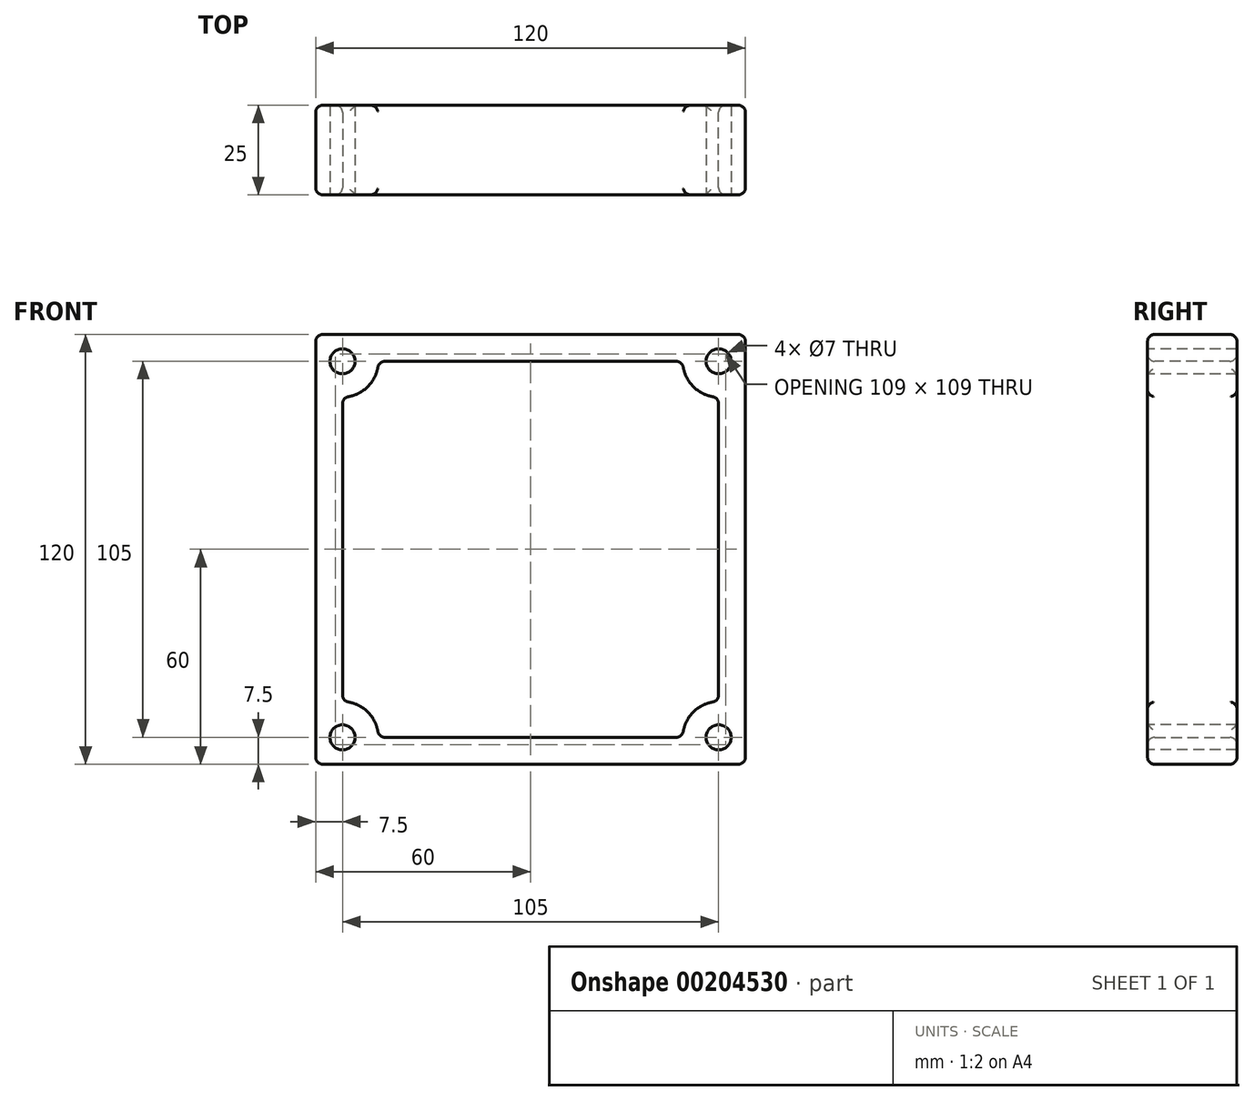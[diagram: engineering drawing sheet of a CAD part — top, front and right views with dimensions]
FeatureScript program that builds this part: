
annotation { "Feature Type Name" : "Feature", "Feature Type Description" : "" }
export const myFeature = defineFeature(function(context is Context, id is Id, definition is map)
    precondition{}
    {
        {
            var Q0;
            Q0=qCreatedBy(makeId("Front.planeOp"),FACE);
            var sketch = newSketch(context, id + "F0", { "sketchPlane" : qUnion([Q0])});
            skLineSegment(sketch, "E0", {"start": v(0, 36.07) * mm, "end": v(0, -63.9) * mm, "construction": true});
            skLineSegment(sketch, "E1", {"start": v(-89.54, 0) * mm, "end": v(99.03, 0) * mm, "construction": true});
            skLineSegment(sketch, "E2.bottom", {"start": v(60, 60) * mm, "end": v(-60, 60) * mm});
            skLineSegment(sketch, "E2.top", {"start": v(60, -60) * mm, "end": v(-60, -60) * mm});
            skLineSegment(sketch, "E2.left", {"start": v(60, 60) * mm, "end": v(60, -60) * mm});
            skLineSegment(sketch, "E2.right", {"start": v(-60, 60) * mm, "end": v(-60, -60) * mm});
            skPoint(sketch, "E2.middle", {"position": v(0, 0) * mm});
            skSolve(sketch);
        }
        {
            var Q0;
            Q0 = qSketchRegion(id + "F0", true);
            extrude(context, id + "F1", {"entities" : qUnion([Q0]), "depth" : 25 * mm});
        }
        {
            var Q0;
            Q0=makeQuery(id+"F1.opExtrude","CAP_FACE",FACE,{"disambiguationData":[OSD([sQuery(id+"F0.wireOp",EDGE,"E2.bottom"),sQuery(id+"F0.wireOp",EDGE,"E2.top"),sQuery(id+"F0.wireOp",EDGE,"E2.left"),sQuery(id+"F0.wireOp",EDGE,"E2.right")])],"isStart":false});
            var sketch = newSketch(context, id + "F2", { "sketchPlane" : qUnion([Q0])});
            skLineSegment(sketch, "E3", {"start": v(-77.64, 0) * mm, "end": v(91.45, 0) * mm, "construction": true});
            skLineSegment(sketch, "E4", {"start": v(0, 68.59) * mm, "end": v(0, -71.2) * mm, "construction": true});
            skCircle(sketch, "E5", {"center": v(-52.5, 52.5) * mm, "radius": 3.5 * mm});
            skCircle(sketch, "E6", {"center": v(-52.5, -52.5) * mm, "radius": 3.5 * mm});
            skCircle(sketch, "E7.MirrorC", {"center": v(52.5, -52.5) * mm, "radius": 3.5 * mm});
            skCircle(sketch, "E8.MirrorC", {"center": v(52.5, 52.5) * mm, "radius": 3.5 * mm});
            skSolve(sketch);
        }
        {
            var Q0;
            Q0 = qSketchRegion(id + "F2", true);
            extrude(context, id + "F3", {"entities" : qUnion([Q0]), "operationType" : NewBodyOperationType.REMOVE, "oppositeDirection" : true, "depth" : 25 * mm});
        }
        {
            var Q0;
            Q0=makeQuery(id+"F1.opExtrude","CAP_FACE",FACE,{"disambiguationData":[OSD([sQuery(id+"F0.wireOp",EDGE,"E2.bottom"),sQuery(id+"F0.wireOp",EDGE,"E2.top"),sQuery(id+"F0.wireOp",EDGE,"E2.left"),sQuery(id+"F0.wireOp",EDGE,"E2.right")])],"isStart":false});
            var sketch = newSketch(context, id + "F4", { "sketchPlane" : qUnion([Q0])});
            skLineSegment(sketch, "E9", {"start": v(0, 67.57) * mm, "end": v(0, -69.58) * mm, "construction": true});
            skLineSegment(sketch, "E10", {"start": v(-83.24, 0) * mm, "end": v(96.08, 0) * mm, "construction": true});
            skLineSegment(sketch, "E11.bottom", {"start": v(42.5, 52.5) * mm, "end": v(-42.5, 52.5) * mm});
            skLineSegment(sketch, "E11.top", {"start": v(42.5, -52.5) * mm, "end": v(-42.5, -52.5) * mm});
            skLineSegment(sketch, "E11.left", {"start": v(52.5, 42.5) * mm, "end": v(52.5, -42.5) * mm});
            skLineSegment(sketch, "E11.right", {"start": v(-52.5, 42.5) * mm, "end": v(-52.5, -42.5) * mm});
            skPoint(sketch, "E11.middle", {"position": v(0, 0) * mm});
            skArc(sketch, "E12", {"start": v(-52.5, 42.5) * mm, "mid": v(-45.43, 45.43) * mm, "end": v(-42.5, 52.5) * mm});
            skArc(sketch, "E13.MirrorC", {"start": v(52.5, 42.5) * mm, "mid": v(45.43, 45.43) * mm, "end": v(42.5, 52.5) * mm});
            skArc(sketch, "E14.MirrorC", {"start": v(-52.5, -42.5) * mm, "mid": v(-45.43, -45.43) * mm, "end": v(-42.5, -52.5) * mm});
            skArc(sketch, "E15.MirrorC", {"start": v(52.5, -42.5) * mm, "mid": v(45.43, -45.43) * mm, "end": v(42.5, -52.5) * mm});
            skPoint(sketch, "E16.orphan", {"position": v(-47.55, 47.55) * mm});
            skPoint(sketch, "E17.orphan", {"position": v(45.43, 45.43) * mm});
            skPoint(sketch, "E18.orphan", {"position": v(47.55, -47.55) * mm});
            skPoint(sketch, "E19.orphan", {"position": v(-45.43, -45.43) * mm});
            skSolve(sketch);
        }
        {
            var Q0;
            Q0 = qSketchRegion(id + "F4", true);
            extrude(context, id + "F5", {"entities" : qUnion([Q0]), "operationType" : NewBodyOperationType.REMOVE, "oppositeDirection" : true, "depth" : 25 * mm});
        }
        {
            var Q0;
            Q0=makeQuery(id+"F1.opExtrude","SWEPT_FACE",FACE,{"disambiguationData":[OSD([sQuery(id+"F0.wireOp",EDGE,"E2.right")])]});
            var Q1;
            Q1=makeQuery(id+"F1.opExtrude","SWEPT_FACE",FACE,{"disambiguationData":[OSD([sQuery(id+"F0.wireOp",EDGE,"E2.bottom")])]});
            var Q2;
            Q2=makeQuery(id+"F1.opExtrude","SWEPT_FACE",FACE,{"disambiguationData":[OSD([sQuery(id+"F0.wireOp",EDGE,"E2.left")])]});
            var Q3;
            Q3=makeQuery(id+"F1.opExtrude","SWEPT_FACE",FACE,{"disambiguationData":[OSD([sQuery(id+"F0.wireOp",EDGE,"E2.top")])]});
            var Q4;
            Q4=makeQuery(id+"F5.boolean.opBoolean","COPY",FACE,{"derivedFrom":makeQuery(id+"F5.opExtrude","SWEPT_FACE",FACE,{"disambiguationData":[OSD([sQuery(id+"F4.wireOp",EDGE,"E11.bottom")])]})});
            var Q5;
            Q5=makeQuery(id+"F5.boolean.opBoolean","COPY",FACE,{"derivedFrom":makeQuery(id+"F5.opExtrude","SWEPT_FACE",FACE,{"disambiguationData":[OSD([sQuery(id+"F4.wireOp",EDGE,"E11.right")])]})});
            var Q6;
            Q6=makeQuery(id+"F5.boolean.opBoolean","COPY",FACE,{"derivedFrom":makeQuery(id+"F5.opExtrude","SWEPT_FACE",FACE,{"disambiguationData":[OSD([sQuery(id+"F4.wireOp",EDGE,"E11.left")])]})});
            var Q7;
            Q7=makeQuery(id+"F5.boolean.opBoolean","COPY",FACE,{"derivedFrom":makeQuery(id+"F5.opExtrude","SWEPT_FACE",FACE,{"disambiguationData":[OSD([sQuery(id+"F4.wireOp",EDGE,"E11.top")])]})});
            fillet(context, id + "F6", {"entities" : qUnion([Q0, Q1, Q2, Q3, Q4, Q5, Q6, Q7]), "radius" : 2 * mm, "tangentPropagation" : true, "allowEdgeOverflow" : false});
        }
    });
